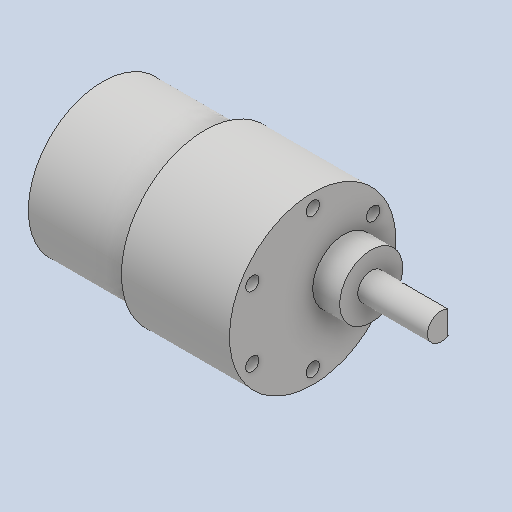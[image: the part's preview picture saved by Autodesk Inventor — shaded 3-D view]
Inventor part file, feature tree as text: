
AUTODESK INVENTOR PART (.ipt)
format: ipt  version: 2023 (Build 270158000, 158)  size: 166,912 bytes
history: native  units: mm
features: extrude x6, sketch x6
ambient origin geometry x8: Origin, YZ Plane, XZ Plane, XY Plane, X Axis, Y Axis, Z Axis, Center Point
bodies: Solid1 (feature_tree)
feature tree (12):
  extrude  "Extrusion1"  Depth=22.7mm TaperAngle=0.0deg
  extrude  "Extrusion2"  Depth=24.0mm TaperAngle=0.0deg
  extrude  "Extrusion3"  Depth=7.0mm
  extrude  "Extrusion4"  Depth=6.0mm
  extrude  "Extrusion5"  Depth=3.0mm
  extrude  "Extrusion6"  Depth=10.0mm TaperAngle=360.0deg
  sketch  "Sketch1"  dims[d0=33.0mm d1=22.7mm d2=0.0mm]
  sketch  "Sketch2"  dims[d3=37.0mm d4=24.0mm d5=0.0mm]
  sketch  "Sketch3"  dims[d6=14.0mm d7=7.0mm]
  sketch  "Sketch4"  dims[d8=6.0mm d9=0.0mm d10=6.0mm]
  sketch  "Sketch5"  dims[d11=15.5mm d12=0.0mm d13=3.0mm]
  sketch  "Sketch6"  dims[d14=15.5mm d15=60.0mm d17=360.0deg d19=10.0mm d20=0.0mm d21=10.0mm d22=0.0mm]
